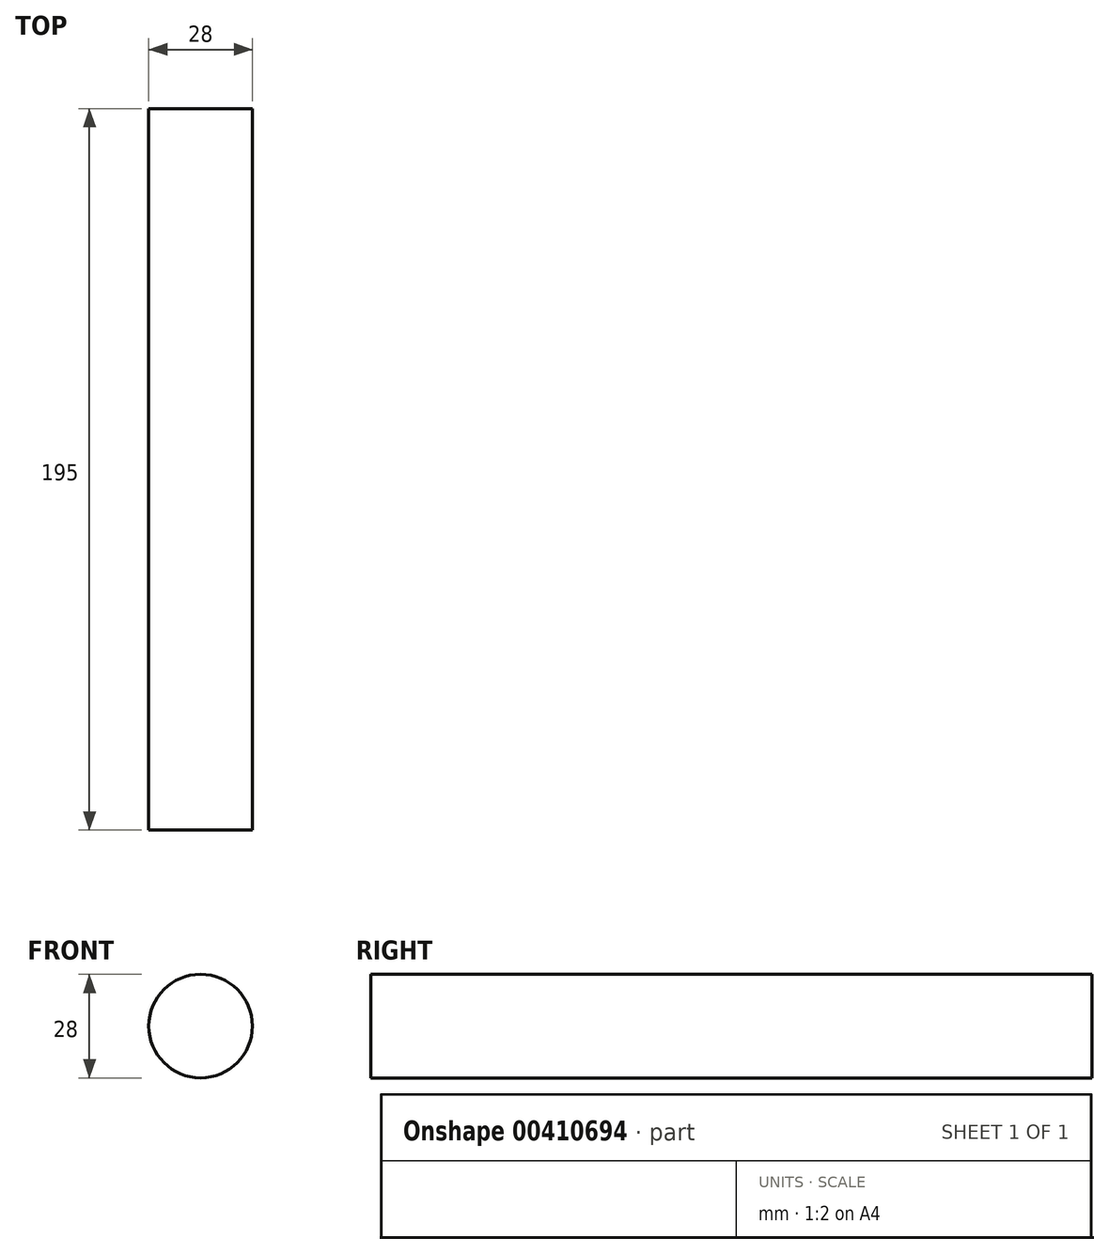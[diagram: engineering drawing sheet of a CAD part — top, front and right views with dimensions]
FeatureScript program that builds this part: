
annotation { "Feature Type Name" : "Feature", "Feature Type Description" : "" }
export const myFeature = defineFeature(function(context is Context, id is Id, definition is map)
    precondition{}
    {
        {
            var Q0;
            Q0=qCreatedBy(makeId("Front.planeOp"),FACE);
            var sketch = newSketch(context, id + "F0", { "sketchPlane" : qUnion([Q0])});
            skCircle(sketch, "E0", {"center": v(0, 0) * mm, "radius": 14 * mm});
            skSolve(sketch);
        }
        {
            var Q0;
            Q0=makeQuery(id+"F0.imprint","IMPRINT",FACE,{"disambiguationData":[TD([[makeQuery(id+"F0.imprint","IMPRINT",EDGE,{"derivedFrom":sQuery(id+"F0.wireOp",EDGE,"E0")}),1.0]])]});
            extrude(context, id + "F1", {"entities" : qUnion([Q0]), "depth" : 195 * mm});
        }
    });
